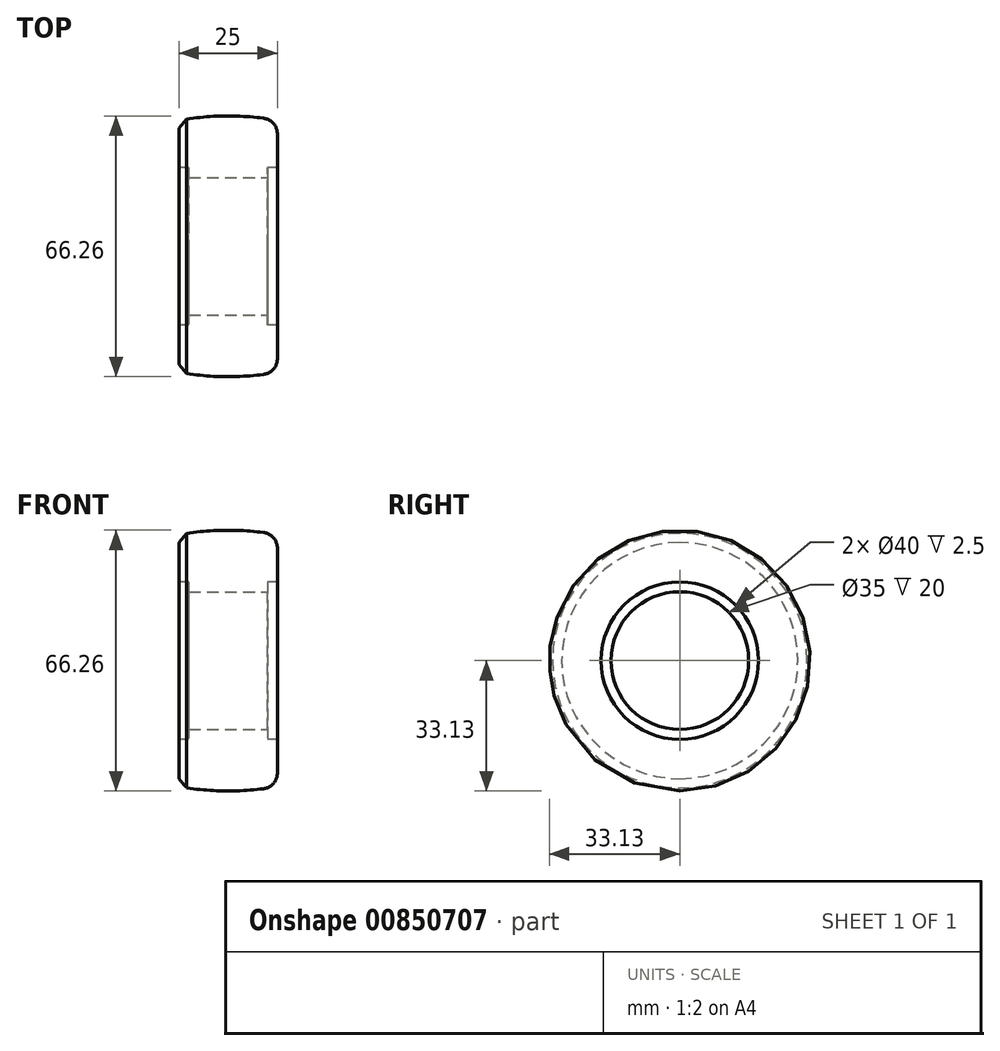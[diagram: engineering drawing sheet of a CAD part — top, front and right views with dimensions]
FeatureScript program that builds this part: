
annotation { "Feature Type Name" : "Feature", "Feature Type Description" : "" }
export const myFeature = defineFeature(function(context is Context, id is Id, definition is map)
    precondition{}
    {
        {
            var Q0;
            Q0=qCreatedBy(makeId("Top.planeOp"),FACE);
            var sketch = newSketch(context, id + "F0", { "sketchPlane" : qUnion([Q0])});
            skLineSegment(sketch, "E0", {"start": v(-10, 0) * mm, "end": v(-10, 20) * mm});
            skLineSegment(sketch, "E1", {"start": v(-10, 20) * mm, "end": v(-12.5, 20) * mm});
            skLineSegment(sketch, "E2", {"start": v(10, 0) * mm, "end": v(10, 20) * mm});
            skLineSegment(sketch, "E3", {"start": v(10, 20) * mm, "end": v(12.5, 20) * mm});
            skLineSegment(sketch, "E4", {"start": v(-12.5, 20) * mm, "end": v(-12.5, 32) * mm});
            skLineSegment(sketch, "E5", {"start": v(12.5, 32) * mm, "end": v(12.5, 20) * mm});
            skLineSegment(sketch, "E6", {"start": v(-10, 0) * mm, "end": v(10, 0) * mm});
            skArc(sketch, "E7", {"start": v(12.5, 32) * mm, "mid": v(0, 33.13) * mm, "end": v(-12.5, 32) * mm});
            skSolve(sketch);
        }
        {
            var Q0;
            Q0 = qSketchRegion(id + "F0", true);
            var Q1;
            Q1=sQuery(id+"F0.wireOp",EDGE,"E6");
            revolve(context, id + "F1", {"surfaceOperationType" : NewSurfaceOperationType.NEW, "entities" : qUnion([Q0]), "axis" : qUnion([Q1]), "revolveType" : RevolveType.FULL});
        }
        {
            var Q0;
            Q0=makeQuery(id+"F1.opRevolve","SWEPT_FACE",FACE,{"disambiguationData":[OSD([sQuery(id+"F0.wireOp",EDGE,"E2")])]});
            var sketch = newSketch(context, id + "F2", { "sketchPlane" : qUnion([Q0])});
            skCircle(sketch, "E8", {"center": v(0, 0) * mm, "radius": 17.5 * mm});
            skSolve(sketch);
        }
        {
            var Q0;
            Q0 = qSketchRegion(id + "F2", true);
            extrude(context, id + "F3", {"entities" : qUnion([Q0]), "operationType" : NewBodyOperationType.REMOVE, "endBound" : BoundingType.UP_TO_NEXT, "oppositeDirection" : true, "depth" : 25 * mm, "offsetDistance" : 25 * mm});
        }
        {
            var Q0;
            Q0=makeQuery(id+"F1.opRevolve","SWEPT_EDGE",EDGE,{"disambiguationData":[OSD([sQuery(id+"F0.wireOp",EDGE,"E5"),sQuery(id+"F0.wireOp",EDGE,"E7")])]});
            fillet(context, id + "F4", {"entities" : qUnion([Q0]), "radius" : 4 * mm, "tangentPropagation" : true, "allowEdgeOverflow" : false});
        }
        {
            var Q0;
            Q0=makeQuery(id+"F1.opRevolve","SWEPT_EDGE",EDGE,{"disambiguationData":[OSD([sQuery(id+"F0.wireOp",EDGE,"E4"),sQuery(id+"F0.wireOp",EDGE,"E7")])]});
            chamfer(context, id + "F5", {"entities" : qUnion([Q0]), "width" : 2 * mm, "tangentPropagation" : true});
        }
    });
